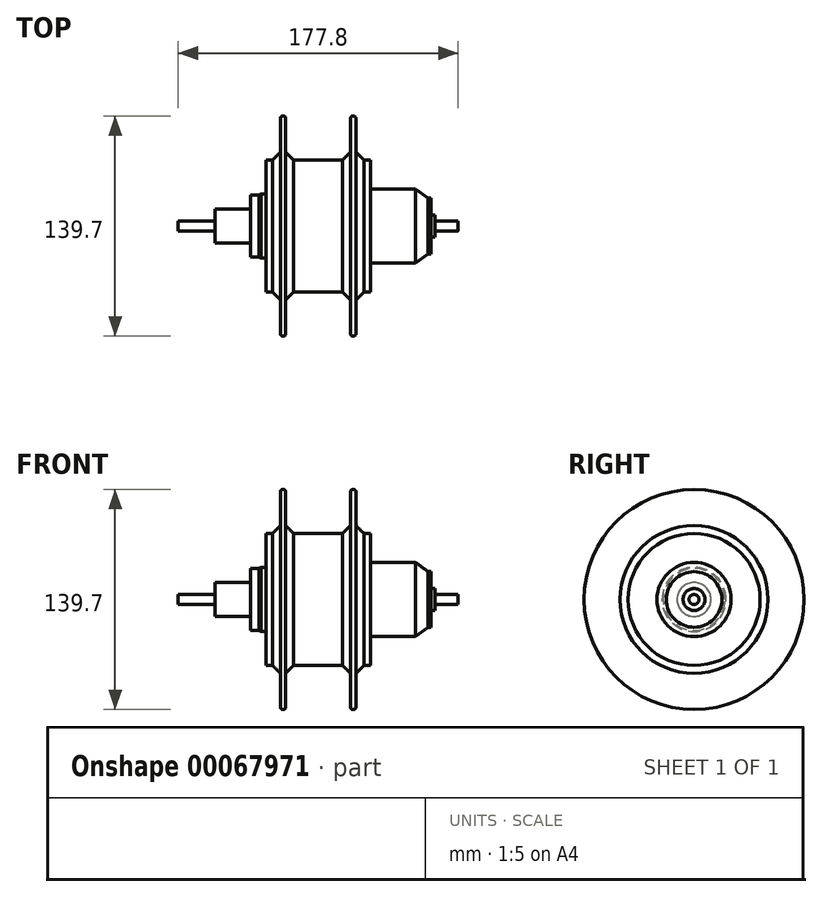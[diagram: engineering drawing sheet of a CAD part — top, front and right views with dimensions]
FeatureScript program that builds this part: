
annotation { "Feature Type Name" : "Feature", "Feature Type Description" : "" }
export const myFeature = defineFeature(function(context is Context, id is Id, definition is map)
    precondition{}
    {
        {
            var Q0;
            Q0=qCreatedBy(makeId("Right.planeOp"),FACE);
            var sketch = newSketch(context, id + "F0", { "sketchPlane" : qUnion([Q0])});
            skCircle(sketch, "E0", {"center": v(0, 0) * mm, "radius": 3.18 * mm});
            skSolve(sketch);
        }
        {
            var Q0;
            Q0=makeQuery(id+"F0.imprint","IMPRINT",FACE,{"disambiguationData":[TD([[makeQuery(id+"F0.imprint","IMPRINT",EDGE,{"derivedFrom":sQuery(id+"F0.wireOp",EDGE,"E0")}),1.0]])]});
            extrude(context, id + "F1", {"entities" : qUnion([Q0]), "endBound" : BoundingType.SYMMETRIC, "depth" : 177.8 * mm});
        }
        {
            var Q0;
            Q0=qCreatedBy(makeId("Front.planeOp"),FACE);
            var sketch = newSketch(context, id + "F2", { "sketchPlane" : qUnion([Q0])});
            skLineSegment(sketch, "E1", {"start": v(0, 0) * mm, "end": v(0, 41.9) * mm, "construction": true});
            skLineSegment(sketch, "E2.0", {"start": v(-88.9, 3.18) * mm, "end": v(-88.9, -3.18) * mm});
            skLineSegment(sketch, "E2.1", {"start": v(88.9, 3.18) * mm, "end": v(88.9, -3.18) * mm});
            skLineSegment(sketch, "E3", {"start": v(-65.57, 3.18) * mm, "end": v(74.13, 3.18) * mm});
            skLineSegment(sketch, "E4", {"start": v(74.13, 3.18) * mm, "end": v(74.13, 6.99) * mm});
            skLineSegment(sketch, "E5", {"start": v(74.13, 6.99) * mm, "end": v(71.55, 6.99) * mm});
            skLineSegment(sketch, "E6", {"start": v(71.55, 6.99) * mm, "end": v(71.55, 17.65) * mm});
            skLineSegment(sketch, "E7", {"start": v(71.55, 17.65) * mm, "end": v(69.83, 17.65) * mm});
            skLineSegment(sketch, "E8", {"start": v(69.83, 17.65) * mm, "end": v(61.84, 23.56) * mm});
            skLineSegment(sketch, "E9", {"start": v(61.84, 23.56) * mm, "end": v(33.2, 23.56) * mm});
            skLineSegment(sketch, "E10", {"start": v(33.2, 23.56) * mm, "end": v(33.2, 41.9) * mm});
            skLineSegment(sketch, "E11", {"start": v(33.2, 41.91) * mm, "end": v(23.92, 41.9) * mm});
            skLineSegment(sketch, "E12", {"start": v(23.92, 41.9) * mm, "end": v(23.92, 69.85) * mm});
            skLineSegment(sketch, "E13", {"start": v(23.92, 69.85) * mm, "end": v(20.62, 69.85) * mm});
            skLineSegment(sketch, "E14", {"start": v(20.62, 69.85) * mm, "end": v(20.62, 41.9) * mm});
            skLineSegment(sketch, "E15", {"start": v(20.62, 41.9) * mm, "end": v(-20.62, 41.9) * mm});
            skLineSegment(sketch, "E16", {"start": v(-20.62, 41.9) * mm, "end": v(-20.62, 69.85) * mm});
            skLineSegment(sketch, "E17", {"start": v(-20.62, 69.85) * mm, "end": v(-23.92, 69.85) * mm});
            skLineSegment(sketch, "E18", {"start": v(-23.92, 69.85) * mm, "end": v(-23.92, 41.9) * mm});
            skLineSegment(sketch, "E19", {"start": v(-23.92, 41.9) * mm, "end": v(-33.2, 41.9) * mm});
            skLineSegment(sketch, "E20", {"start": v(-33.2, 41.9) * mm, "end": v(-33.2, 20.32) * mm});
            skLineSegment(sketch, "E21", {"start": v(-33.2, 20.32) * mm, "end": v(-36.42, 20.32) * mm});
            skLineSegment(sketch, "E22", {"start": v(-36.42, 20.32) * mm, "end": v(-37.5, 19.68) * mm});
            skLineSegment(sketch, "E23", {"start": v(-37.5, 19.69) * mm, "end": v(-43.03, 19.69) * mm});
            skLineSegment(sketch, "E24", {"start": v(-43.03, 19.69) * mm, "end": v(-43.03, 10.79) * mm});
            skLineSegment(sketch, "E25", {"start": v(-43.03, 10.79) * mm, "end": v(-65.57, 10.79) * mm});
            skLineSegment(sketch, "E26", {"start": v(-65.57, 10.79) * mm, "end": v(-65.57, 3.18) * mm});
            skLineSegment(sketch, "E27", {"start": v(0, 0) * mm, "end": v(108.81, 0) * mm, "construction": true});
            skSolve(sketch);
        }
        {
            var Q0;
            Q0 = qSketchRegion(id + "F2", true);
            var Q1;
            Q1=sQuery(id+"F2.wireOp",EDGE,"E27");
            revolve(context, id + "F3", {"operationType" : NewBodyOperationType.ADD, "entities" : qUnion([Q0]), "axis" : qUnion([Q1]), "revolveType" : RevolveType.FULL});
        }
        {
            var Q0;
            Q0=makeQuery(id+"F3.opRevolve","SWEPT_EDGE",EDGE,{"disambiguationData":[OSD([sQuery(id+"F2.wireOp",EDGE,"E15"),sQuery(id+"F2.wireOp",EDGE,"E16")])]});
            var Q1;
            Q1=makeQuery(id+"F3.opRevolve","SWEPT_EDGE",EDGE,{"disambiguationData":[OSD([sQuery(id+"F2.wireOp",EDGE,"E11"),sQuery(id+"F2.wireOp",EDGE,"E12")])]});
            var Q2;
            Q2=makeQuery(id+"F3.opRevolve","SWEPT_EDGE",EDGE,{"disambiguationData":[OSD([sQuery(id+"F2.wireOp",EDGE,"E14"),sQuery(id+"F2.wireOp",EDGE,"E15")])]});
            var Q3;
            Q3=makeQuery(id+"F3.opRevolve","SWEPT_EDGE",EDGE,{"disambiguationData":[OSD([sQuery(id+"F2.wireOp",EDGE,"E18"),sQuery(id+"F2.wireOp",EDGE,"E19")])]});
            chamfer(context, id + "F4", {"entities" : qUnion([Q0, Q1, Q2, Q3]), "width" : 5.08 * mm, "tangentPropagation" : true});
        }
        {
            var Q0;
            Q0=makeQuery(id+"F3.opRevolve","SWEPT_EDGE",EDGE,{"disambiguationData":[OSD([sQuery(id+"F2.wireOp",EDGE,"E9"),sQuery(id+"F2.wireOp",EDGE,"E10")])]});
            var Q1;
            Q1=makeQuery(id+"F3.opRevolve","SWEPT_EDGE",EDGE,{"disambiguationData":[OSD([sQuery(id+"F2.wireOp",EDGE,"E24"),sQuery(id+"F2.wireOp",EDGE,"E25")])]});
            var Q2;
            Q2=makeQuery(id+"F3.opRevolve","SWEPT_EDGE",EDGE,{"disambiguationData":[OSD([sQuery(id+"F2.wireOp",EDGE,"E3"),sQuery(id+"F2.wireOp",EDGE,"E26")])]});
            var Q3;
            Q3=makeQuery(id+"F3.opRevolve","SWEPT_EDGE",EDGE,{"disambiguationData":[OSD([sQuery(id+"F2.wireOp",EDGE,"E17"),sQuery(id+"F2.wireOp",EDGE,"E18")])]});
            var Q4;
            Q4=makeQuery(id+"F3.opRevolve","SWEPT_EDGE",EDGE,{"disambiguationData":[OSD([sQuery(id+"F2.wireOp",EDGE,"E16"),sQuery(id+"F2.wireOp",EDGE,"E17")])]});
            var Q5;
            Q5=makeQuery(id+"F3.opRevolve","SWEPT_EDGE",EDGE,{"disambiguationData":[OSD([sQuery(id+"F2.wireOp",EDGE,"E13"),sQuery(id+"F2.wireOp",EDGE,"E14")])]});
            var Q6;
            Q6=makeQuery(id+"F3.opRevolve","SWEPT_EDGE",EDGE,{"disambiguationData":[OSD([sQuery(id+"F2.wireOp",EDGE,"E12"),sQuery(id+"F2.wireOp",EDGE,"E13")])]});
            fillet(context, id + "F5", {"entities" : qUnion([Q0, Q1, Q2, Q3, Q4, Q5, Q6]), "radius" : 1.27 * mm, "tangentPropagation" : true, "allowEdgeOverflow" : false});
        }
    });
